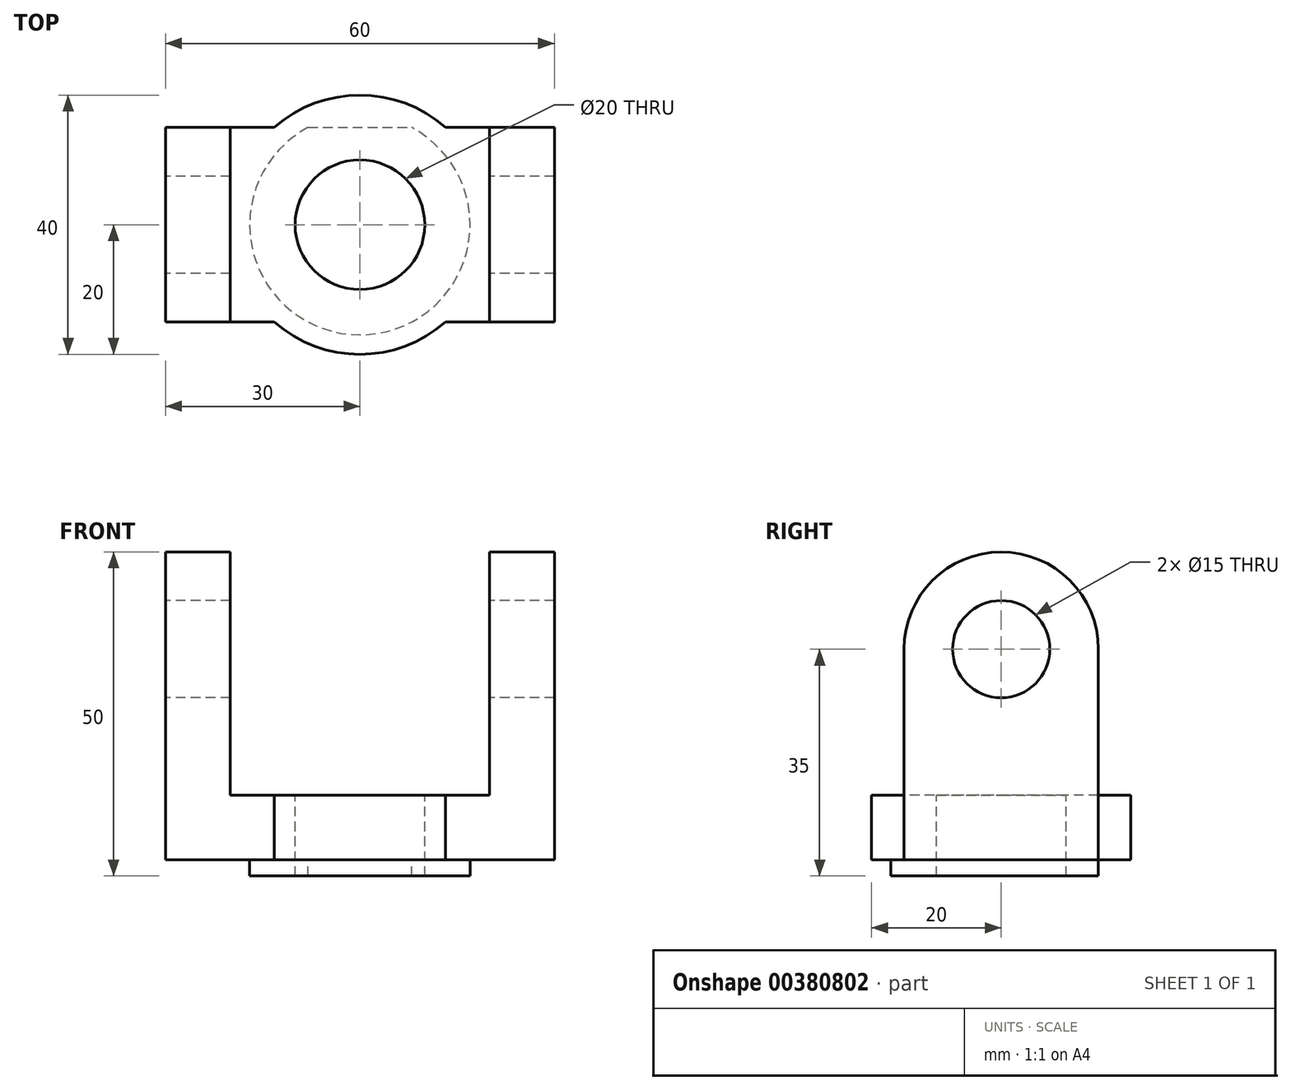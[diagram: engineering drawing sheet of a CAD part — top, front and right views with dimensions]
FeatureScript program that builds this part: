
annotation { "Feature Type Name" : "Feature", "Feature Type Description" : "" }
export const myFeature = defineFeature(function(context is Context, id is Id, definition is map)
    precondition{}
    {
        {
            var Q0;
            Q0=qCreatedBy(makeId("Top.planeOp"),FACE);
            var sketch = newSketch(context, id + "F0", { "sketchPlane" : qUnion([Q0])});
            skLineSegment(sketch, "E0.bottom", {"start": v(-30, 15) * mm, "end": v(30, 15) * mm});
            skLineSegment(sketch, "E0.top", {"start": v(-30, -15) * mm, "end": v(30, -15) * mm});
            skLineSegment(sketch, "E0.left", {"start": v(-30, 15) * mm, "end": v(-30, -15) * mm});
            skLineSegment(sketch, "E0.right", {"start": v(30, 15) * mm, "end": v(30, -15) * mm});
            skSolve(sketch);
        }
        {
            var Q0;
            Q0 = qSketchRegion(id + "F0", true);
            extrude(context, id + "F1", {"entities" : qUnion([Q0]), "depth" : 10 * mm});
        }
        {
            var Q0;
            Q0=makeQuery(id+"F1.opExtrude","CAP_FACE",FACE,{"disambiguationData":[OSD([sQuery(id+"F0.wireOp",EDGE,"E0.bottom"),sQuery(id+"F0.wireOp",EDGE,"E0.top"),sQuery(id+"F0.wireOp",EDGE,"E0.left"),sQuery(id+"F0.wireOp",EDGE,"E0.right")])],"isStart":false});
            var sketch = newSketch(context, id + "F2", { "sketchPlane" : qUnion([Q0])});
            skLineSegment(sketch, "E1.bottom", {"start": v(-30, 15) * mm, "end": v(-20, 15) * mm});
            skLineSegment(sketch, "E1.top", {"start": v(-30, -15) * mm, "end": v(-20, -15) * mm});
            skLineSegment(sketch, "E1.left", {"start": v(-30, 15) * mm, "end": v(-30, -15) * mm});
            skLineSegment(sketch, "E1.right", {"start": v(-20, 15) * mm, "end": v(-20, -15) * mm});
            skLineSegment(sketch, "E2.bottom", {"start": v(30, 15) * mm, "end": v(20, 15) * mm});
            skLineSegment(sketch, "E2.top", {"start": v(30, -15) * mm, "end": v(20, -15) * mm});
            skLineSegment(sketch, "E2.left", {"start": v(30, 15) * mm, "end": v(30, -15) * mm});
            skLineSegment(sketch, "E2.right", {"start": v(20, 15) * mm, "end": v(20, -15) * mm});
            skSolve(sketch);
        }
        {
            var Q0;
            Q0 = qSketchRegion(id + "F2", true);
            extrude(context, id + "F3", {"entities" : qUnion([Q0]), "operationType" : NewBodyOperationType.ADD, "depth" : 37.5 * mm});
        }
        {
            var Q0;
            Q0=makeQuery(id+"F3.boolean.opBoolean","MERGE",FACE,{"derivedFrom":[makeQuery(id+"F1.opExtrude","SWEPT_FACE",FACE,{"disambiguationData":[OSD([sQuery(id+"F0.wireOp",EDGE,"E0.left")])]}),makeQuery(id+"F3.opExtrude","SWEPT_FACE",FACE,{"disambiguationData":[OSD([sQuery(id+"F2.wireOp",EDGE,"E1.left")])]})]});
            var sketch = newSketch(context, id + "F4", { "sketchPlane" : qUnion([Q0])});
            skArc(sketch, "E3", {"start": v(15, 32.5) * mm, "mid": v(0, 47.5) * mm, "end": v(-15, 32.5) * mm});
            skLineSegment(sketch, "E4", {"start": v(-15, 32.5) * mm, "end": v(-15, 47.5) * mm});
            skLineSegment(sketch, "E5", {"start": v(-15, 47.5) * mm, "end": v(0, 47.5) * mm});
            skLineSegment(sketch, "E6", {"start": v(0, 47.5) * mm, "end": v(15, 47.5) * mm});
            skLineSegment(sketch, "E7", {"start": v(15, 47.5) * mm, "end": v(15, 32.5) * mm});
            skSolve(sketch);
        }
        {
            var Q0;
            {var subQ0=sQuery(id+"F4.wireOp",EDGE,"E4");Q0=makeQuery(id+"F4.imprint","IMPRINT",FACE,{"disambiguationData":[TD([[makeQuery(id+"F4.imprint","IMPRINT",EDGE,{"derivedFrom":subQ0}),1.0]])]});}
            var Q1;
            {var subQ2=sQuery(id+"F4.wireOp",EDGE,"E6");Q1=makeQuery(id+"F4.imprint","IMPRINT",FACE,{"disambiguationData":[TD([[makeQuery(id+"F4.imprint","IMPRINT",EDGE,{"derivedFrom":subQ2}),-1.0]])]});}
            extrude(context, id + "F5", {"entities" : qUnion([Q0, Q1]), "operationType" : NewBodyOperationType.REMOVE, "endBound" : BoundingType.THROUGH_ALL, "oppositeDirection" : true, "depth" : 25 * mm});
        }
        {
            var Q0;
            Q0=makeQuery(id+"F3.boolean.opBoolean","MERGE",FACE,{"derivedFrom":[makeQuery(id+"F1.opExtrude","SWEPT_FACE",FACE,{"disambiguationData":[OSD([sQuery(id+"F0.wireOp",EDGE,"E0.left")])]}),makeQuery(id+"F3.opExtrude","SWEPT_FACE",FACE,{"disambiguationData":[OSD([sQuery(id+"F2.wireOp",EDGE,"E1.left")])]})]});
            var sketch = newSketch(context, id + "F6", { "sketchPlane" : qUnion([Q0])});
            skCircle(sketch, "E8", {"center": v(0, 32.5) * mm, "radius": 7.5 * mm});
            skSolve(sketch);
        }
        {
            var Q0;
            Q0=makeQuery(id+"F6.imprint","IMPRINT",FACE,{"disambiguationData":[TD([[makeQuery(id+"F6.imprint","IMPRINT",EDGE,{"derivedFrom":sQuery(id+"F6.wireOp",EDGE,"E8")}),1.0]])]});
            extrude(context, id + "F7", {"entities" : qUnion([Q0]), "operationType" : NewBodyOperationType.REMOVE, "endBound" : BoundingType.THROUGH_ALL, "oppositeDirection" : true, "depth" : 25 * mm});
        }
        {
            var Q0;
            Q0=makeQuery(id+"F1.opExtrude","CAP_FACE",FACE,{"disambiguationData":[OSD([sQuery(id+"F0.wireOp",EDGE,"E0.bottom"),sQuery(id+"F0.wireOp",EDGE,"E0.top"),sQuery(id+"F0.wireOp",EDGE,"E0.left"),sQuery(id+"F0.wireOp",EDGE,"E0.right")])],"isStart":true});
            var sketch = newSketch(context, id + "F8", { "sketchPlane" : qUnion([Q0])});
            skCircle(sketch, "E9", {"center": v(0, 0) * mm, "radius": 17 * mm});
            skSolve(sketch);
        }
        {
            var Q0;
            {var subQ0=sQuery(id+"F8.wireOp",EDGE,"E9");var subQ1=makeQuery(id+"F1.opExtrude","CAP_EDGE",EDGE,{"disambiguationData":[OSD([sQuery(id+"F0.wireOp",EDGE,"E0.top")])],"isStart":true});var subQ2=makeQuery(id+"F8.imprint","INTERSECT",VERTEX,{"disambiguationData":[OD(0.0)],"derivedFrom":[subQ1,subQ0]});Q0=makeQuery(id+"F8.imprint","IMPRINT",FACE,{"disambiguationData":[TD([[makeQuery(id+"F8.imprint","IMPRINT",EDGE,{"disambiguationData":[TD([[subQ2,1.0]])],"derivedFrom":subQ0}),1.0]])]});}
            var Q1;
            {var subQ0=sQuery(id+"F8.wireOp",EDGE,"E9");var subQ1=makeQuery(id+"F1.opExtrude","CAP_EDGE",EDGE,{"disambiguationData":[OSD([sQuery(id+"F0.wireOp",EDGE,"E0.top")])],"isStart":true});var subQ2=makeQuery(id+"F8.imprint","INTERSECT",VERTEX,{"disambiguationData":[OD(0.0)],"derivedFrom":[subQ1,subQ0]});Q1=makeQuery(id+"F8.imprint","IMPRINT",FACE,{"disambiguationData":[TD([[makeQuery(id+"F8.imprint","IMPRINT",EDGE,{"disambiguationData":[TD([[subQ2,-1.0]])],"derivedFrom":subQ0}),1.0]])]});}
            var Q2;
            {var subQ0=sQuery(id+"F8.wireOp",EDGE,"E9");var subQ1=makeQuery(id+"F1.opExtrude","CAP_EDGE",EDGE,{"disambiguationData":[OSD([sQuery(id+"F0.wireOp",EDGE,"E0.bottom")])],"isStart":true});var subQ2=makeQuery(id+"F8.imprint","INTERSECT",VERTEX,{"disambiguationData":[OD(0.0)],"derivedFrom":[subQ1,subQ0]});Q2=makeQuery(id+"F8.imprint","IMPRINT",FACE,{"disambiguationData":[TD([[makeQuery(id+"F8.imprint","IMPRINT",EDGE,{"disambiguationData":[TD([[subQ2,-1.0]])],"derivedFrom":subQ0}),1.0]])]});}
            extrude(context, id + "F9", {"entities" : qUnion([Q0, Q1, Q2]), "operationType" : NewBodyOperationType.ADD, "depth" : 2.5 * mm});
        }
        {
            var Q0;
            Q0=makeQuery(id+"F1.opExtrude","CAP_FACE",FACE,{"disambiguationData":[OSD([sQuery(id+"F0.wireOp",EDGE,"E0.bottom"),sQuery(id+"F0.wireOp",EDGE,"E0.top"),sQuery(id+"F0.wireOp",EDGE,"E0.left"),sQuery(id+"F0.wireOp",EDGE,"E0.right")])],"isStart":false});
            var sketch = newSketch(context, id + "F10", { "sketchPlane" : qUnion([Q0])});
            skArc(sketch, "E10", {"start": v(13.23, 15) * mm, "mid": v(0, 20) * mm, "end": v(-13.23, 15) * mm});
            skArc(sketch, "E11", {"start": v(-13.23, -15) * mm, "mid": v(0, -20) * mm, "end": v(13.23, -15) * mm});
            skLineSegment(sketch, "E12", {"start": v(-13.23, -15) * mm, "end": v(13.23, -15) * mm});
            skLineSegment(sketch, "E13", {"start": v(13.23, 15) * mm, "end": v(-13.23, 15) * mm});
            skSolve(sketch);
        }
        {
            var Q0;
            Q0 = qSketchRegion(id + "F10", true);
            extrude(context, id + "F11", {"entities" : qUnion([Q0]), "operationType" : NewBodyOperationType.ADD, "oppositeDirection" : true, "depth" : 10 * mm});
        }
        {
            var Q0;
            Q0=makeQuery(id+"F11.boolean.opBoolean","MERGE",FACE,{"derivedFrom":[makeQuery(id+"F1.opExtrude","CAP_FACE",FACE,{"disambiguationData":[OSD([sQuery(id+"F0.wireOp",EDGE,"E0.bottom"),sQuery(id+"F0.wireOp",EDGE,"E0.top"),sQuery(id+"F0.wireOp",EDGE,"E0.left"),sQuery(id+"F0.wireOp",EDGE,"E0.right")])],"isStart":false}),makeQuery(id+"F11.opExtrude","CAP_FACE",FACE,{"disambiguationData":[OSD([sQuery(id+"F10.wireOp",EDGE,"E10"),sQuery(id+"F10.wireOp",EDGE,"E13")])],"isStart":true}),makeQuery(id+"F11.opExtrude","CAP_FACE",FACE,{"disambiguationData":[OSD([sQuery(id+"F10.wireOp",EDGE,"E11"),sQuery(id+"F10.wireOp",EDGE,"E12")])],"isStart":true})]});
            var sketch = newSketch(context, id + "F12", { "sketchPlane" : qUnion([Q0])});
            skCircle(sketch, "E14", {"center": v(0, 0) * mm, "radius": 10 * mm});
            skSolve(sketch);
        }
        {
            var Q0;
            Q0 = qSketchRegion(id + "F12", true);
            extrude(context, id + "F13", {"entities" : qUnion([Q0]), "operationType" : NewBodyOperationType.REMOVE, "oppositeDirection" : true, "depth" : 25 * mm});
        }
    });
